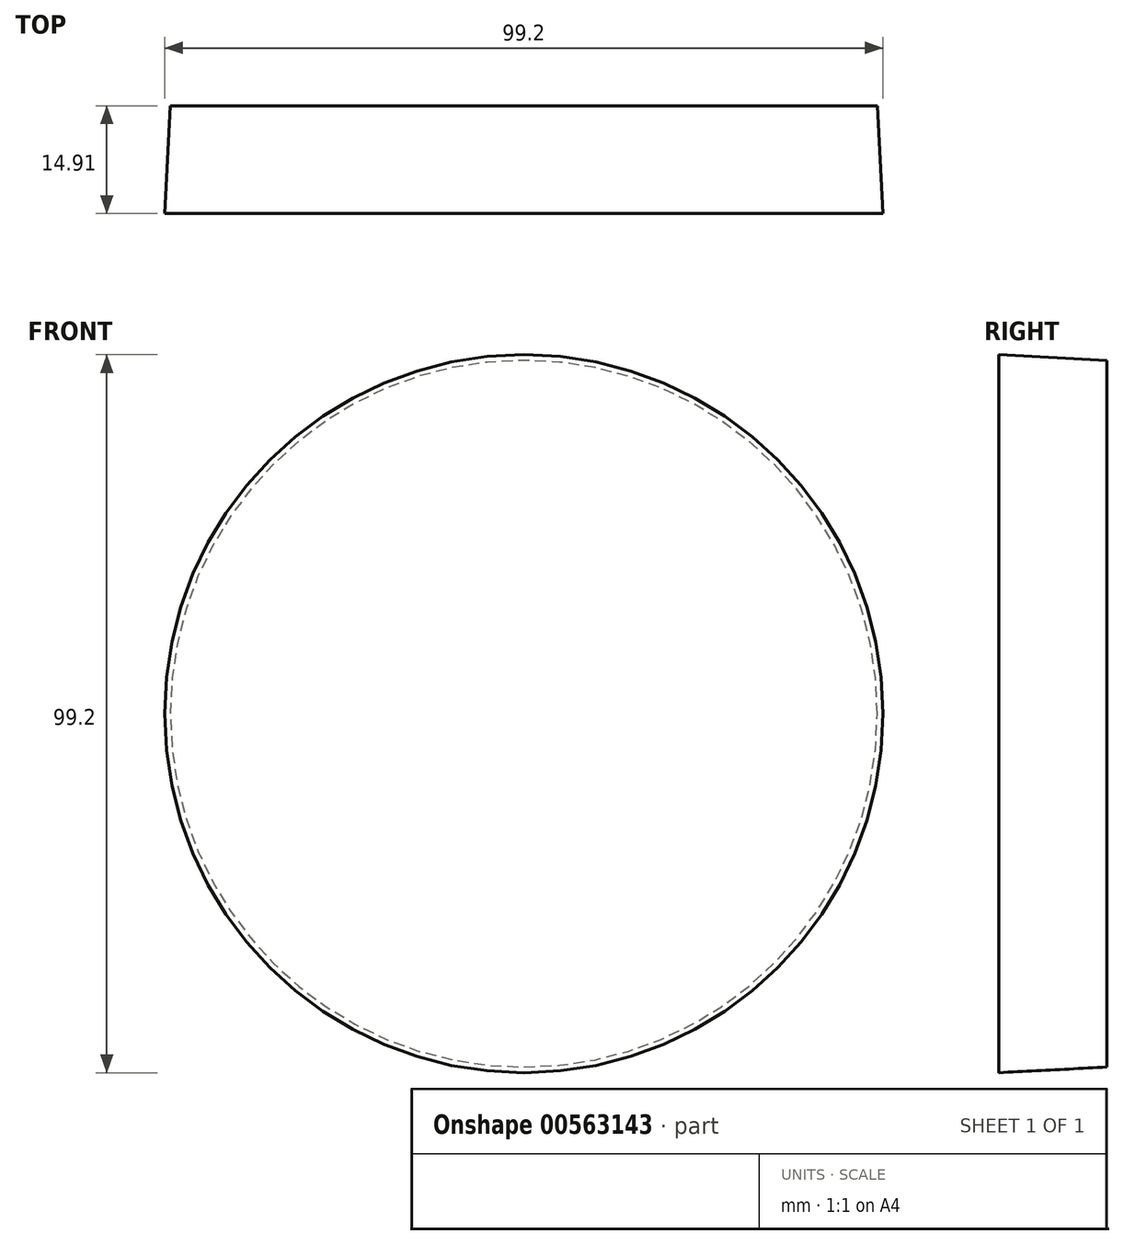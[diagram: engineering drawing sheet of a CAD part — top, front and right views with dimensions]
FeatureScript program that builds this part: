
annotation { "Feature Type Name" : "Feature", "Feature Type Description" : "" }
export const myFeature = defineFeature(function(context is Context, id is Id, definition is map)
    precondition{}
    {
        {
            var Q0;
            Q0=qCreatedBy(makeId("Front.planeOp"),FACE);
            var sketch = newSketch(context, id + "F0", { "sketchPlane" : qUnion([Q0])});
            skCircle(sketch, "E0", {"center": v(0, 22.91) * mm, "radius": 48.82 * mm});
            skSolve(sketch);
        }
        {
            var Q0;
            Q0 = qSketchRegion(id + "F0", true);
            extrude(context, id + "F1", {"entities" : qUnion([Q0]), "depth" : 14.9 * mm, "offsetDistance" : 25.4 * mm, "hasDraft" : true, "draftAngle" : 3 * degree});
        }
    });
